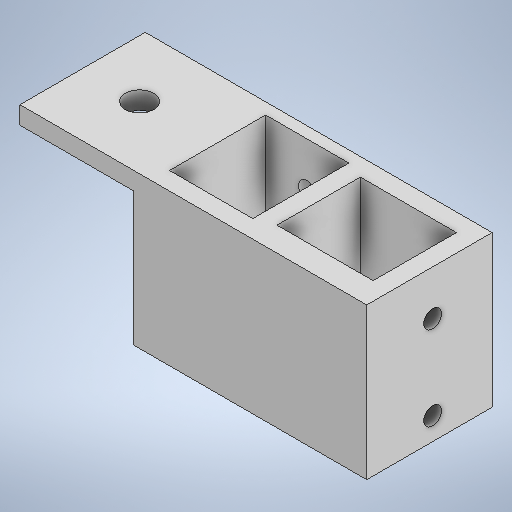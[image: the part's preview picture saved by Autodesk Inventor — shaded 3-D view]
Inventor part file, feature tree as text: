
AUTODESK INVENTOR PART (.ipt)
format: ipt  version: 2025.1 (Build 291241000, 241)  size: 264,192 bytes
history: native  units: in
note: dims shown in document units (in); Inventor stores cm internally (conversion verified against a paired STEP export)
features: extrude x5, sketch x5, direct_edit x1, move_body x1
ambient origin geometry x8: Origin, YZ Plane, XZ Plane, XY Plane, X Axis, Y Axis, Z Axis, Center Point
bodies: Solid1 (feature_tree)
feature tree (12):
  extrude  "Extrusion1"  Depth=0.675in
  extrude  "Extrusion2"  Depth=0.125in
  extrude  "Extrusion3"  Depth=0.585in
  direct_edit  "Direct Edit1"
  extrude  "Extrusion4"  Depth=0.125in
  extrude  "Extrusion5"  Depth=0.125in TaperAngle=0.0deg
  sketch  "Sketch1"  dims[d0=0.585in d1=0.675in]
  sketch  "Sketch2"  dims[d2=0.045in d3=0.125in]
  sketch  "Sketch3"  dims[d4=0.675in d5=0.585in]
  sketch  "Sketch4"  dims[d6=0.125in d7=0.125in]
  sketch  "Sketch5"  dims[d8=0.125in d11=1.0in d12=0.0in d13=0.315in d14=0.125in d15=0.59in d16=0.125in d17=0.375in d18=0.0in d19=0.315in d20=0.125in d21=0.59in d22=0.125in d23=0.375in d24=0.0in d25=0.0in d26=0.0in d27=0.0625in d29=0.8in d30=0.0in d32=0.575in d33=0.0in d34=0.125in d35=0.125in d36=0.125in d39=0.2in]
  move_body  "Move1"
